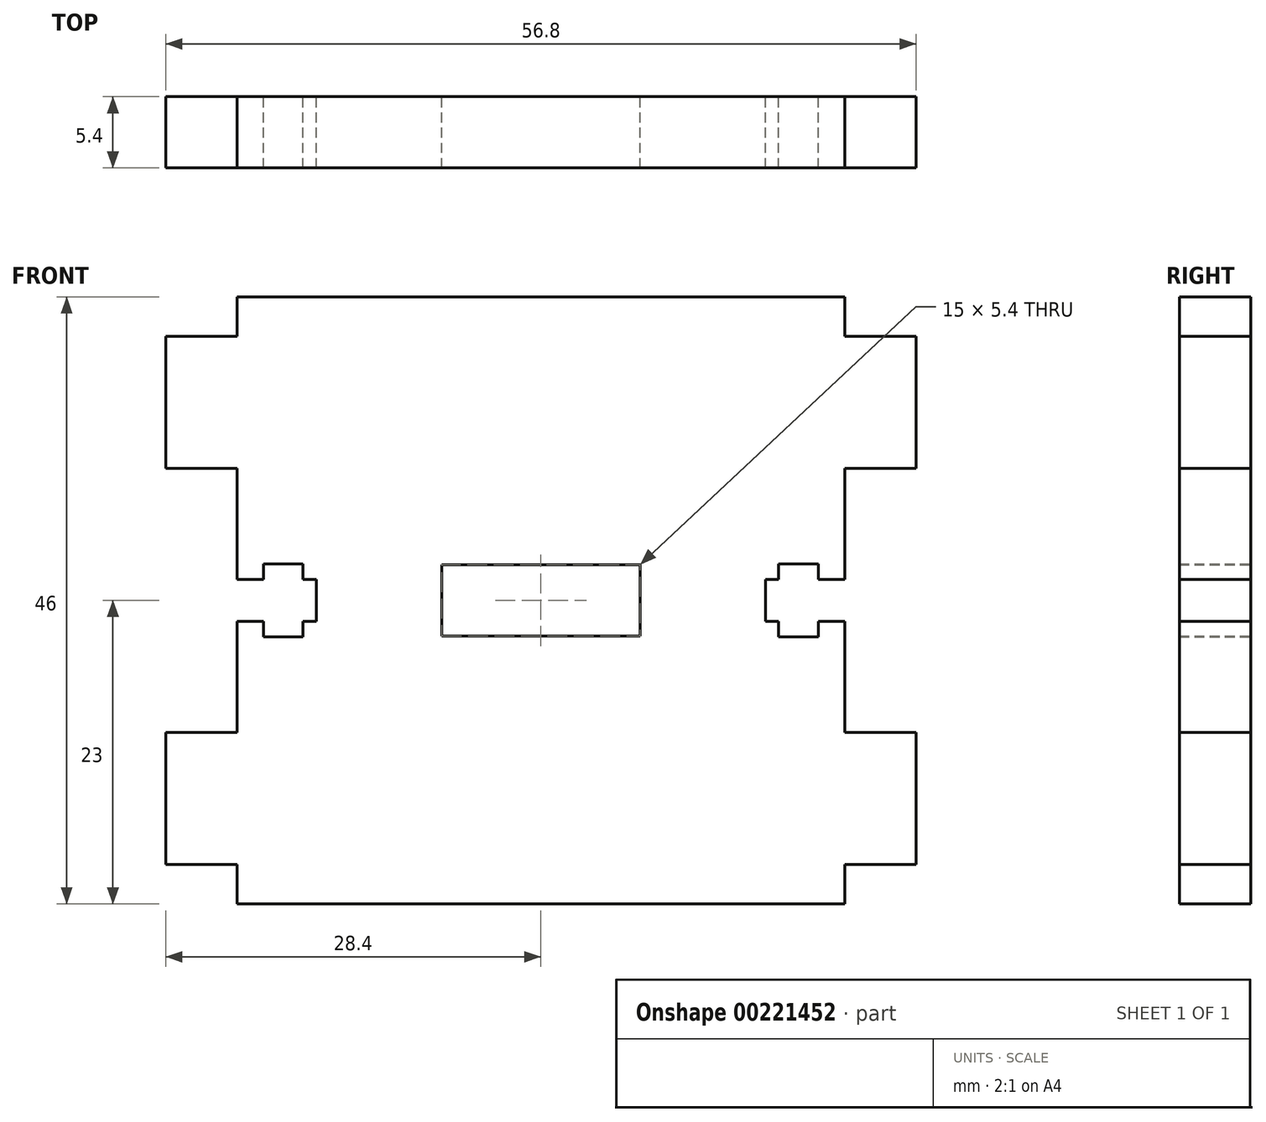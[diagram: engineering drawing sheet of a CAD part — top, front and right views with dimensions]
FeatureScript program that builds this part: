
annotation { "Feature Type Name" : "Feature", "Feature Type Description" : "" }
export const myFeature = defineFeature(function(context is Context, id is Id, definition is map)
    precondition{}
    {
        {
            assignVariable(context, id + "F0", {"name" : "thickness", "anyValue" : 5.4 * mm});
        }
        {
            var Q0;
            Q0=qCreatedBy(makeId("Front.planeOp"),FACE);
            var sketch = newSketch(context, id + "F1", { "sketchPlane" : qUnion([Q0])});
            skLineSegment(sketch, "E0.bottom", {"start": v(0, 0) * mm, "end": v(46, 0) * mm});
            skLineSegment(sketch, "E0.top", {"start": v(0, 46) * mm, "end": v(46, 46) * mm});
            skLineSegment(sketch, "E0.left", {"start": v(0, 0) * mm, "end": v(0, 3) * mm});
            skLineSegment(sketch, "E0.right", {"start": v(46, 0) * mm, "end": v(46, 3) * mm});
            skLineSegment(sketch, "E1", {"start": v(0, 43) * mm, "end": v(-5.4, 43) * mm});
            skLineSegment(sketch, "E2", {"start": v(-5.4, 43) * mm, "end": v(-5.4, 33) * mm});
            skLineSegment(sketch, "E3", {"start": v(-5.4, 33) * mm, "end": v(0, 33) * mm});
            skLineSegment(sketch, "E4", {"start": v(0, 23) * mm, "end": v(46, 23) * mm, "construction": true});
            skLineSegment(sketch, "E5", {"start": v(0, 24.6) * mm, "end": v(2, 24.6) * mm});
            skLineSegment(sketch, "E6", {"start": v(2, 24.6) * mm, "end": v(2, 25.75) * mm});
            skLineSegment(sketch, "E7", {"start": v(2, 25.75) * mm, "end": v(5, 25.75) * mm});
            skLineSegment(sketch, "E8", {"start": v(5, 25.75) * mm, "end": v(5, 24.6) * mm});
            skLineSegment(sketch, "E9", {"start": v(5, 24.6) * mm, "end": v(6, 24.6) * mm});
            skLineSegment(sketch, "E10", {"start": v(6, 24.6) * mm, "end": v(6, 23) * mm});
            skLineSegment(sketch, "E11.MirrorCS", {"start": v(-5.4, 3) * mm, "end": v(-5.4, 13) * mm});
            skLineSegment(sketch, "E12.MirrorCS", {"start": v(-5.4, 13) * mm, "end": v(0, 13) * mm});
            skLineSegment(sketch, "E13.MirrorCS", {"start": v(0, 3) * mm, "end": v(-5.4, 3) * mm});
            skLineSegment(sketch, "E14.MirrorCS", {"start": v(5, 21.4) * mm, "end": v(6, 21.4) * mm});
            skLineSegment(sketch, "E15.MirrorCS", {"start": v(5, 20.25) * mm, "end": v(5, 21.4) * mm});
            skLineSegment(sketch, "E16.MirrorCS", {"start": v(2, 20.25) * mm, "end": v(5, 20.25) * mm});
            skLineSegment(sketch, "E17.MirrorCS", {"start": v(2, 21.4) * mm, "end": v(2, 20.25) * mm});
            skLineSegment(sketch, "E18.MirrorCS", {"start": v(6, 21.4) * mm, "end": v(6, 23) * mm});
            skLineSegment(sketch, "E19.MirrorCS", {"start": v(0, 21.4) * mm, "end": v(2, 21.4) * mm});
            skLineSegment(sketch, "E20.trimOffspring", {"start": v(0, 24.6) * mm, "end": v(0, 33) * mm});
            skLineSegment(sketch, "E21.trimOffspring", {"start": v(0, 43) * mm, "end": v(0, 46) * mm});
            skLineSegment(sketch, "E22.trimOffspring", {"start": v(0, 13) * mm, "end": v(0, 21.4) * mm});
            skLineSegment(sketch, "E23", {"start": v(0, 24.6) * mm, "end": v(0, 21.4) * mm, "construction": true});
            skLineSegment(sketch, "E24", {"start": v(23, 46) * mm, "end": v(23, 0) * mm, "construction": true});
            skLineSegment(sketch, "E25.MirrorCS", {"start": v(51.4, 43) * mm, "end": v(51.4, 33) * mm});
            skLineSegment(sketch, "E26.MirrorCS", {"start": v(51.4, 33) * mm, "end": v(46, 33) * mm});
            skLineSegment(sketch, "E27.MirrorCS", {"start": v(46, 43) * mm, "end": v(51.4, 43) * mm});
            skLineSegment(sketch, "E28.MirrorCS", {"start": v(41, 20.25) * mm, "end": v(41, 21.4) * mm});
            skLineSegment(sketch, "E29.MirrorCS", {"start": v(41, 24.6) * mm, "end": v(40, 24.6) * mm});
            skLineSegment(sketch, "E30.MirrorCS", {"start": v(41, 25.75) * mm, "end": v(41, 24.6) * mm});
            skLineSegment(sketch, "E31.MirrorCS", {"start": v(44, 24.6) * mm, "end": v(44, 25.75) * mm});
            skLineSegment(sketch, "E32.MirrorCS", {"start": v(46, 24.6) * mm, "end": v(44, 24.6) * mm});
            skLineSegment(sketch, "E33.MirrorCS", {"start": v(46, 21.4) * mm, "end": v(44, 21.4) * mm});
            skLineSegment(sketch, "E34.MirrorCS", {"start": v(44, 21.4) * mm, "end": v(44, 20.25) * mm});
            skLineSegment(sketch, "E35.MirrorCS", {"start": v(40, 21.4) * mm, "end": v(40, 23) * mm});
            skLineSegment(sketch, "E36.MirrorCS", {"start": v(41, 21.4) * mm, "end": v(40, 21.4) * mm});
            skLineSegment(sketch, "E37.MirrorCS", {"start": v(40, 24.6) * mm, "end": v(40, 23) * mm});
            skLineSegment(sketch, "E38.MirrorCS", {"start": v(44, 25.75) * mm, "end": v(41, 25.75) * mm});
            skLineSegment(sketch, "E39.MirrorCS", {"start": v(44, 20.25) * mm, "end": v(41, 20.25) * mm});
            skLineSegment(sketch, "E40.MirrorCS", {"start": v(51.4, 3) * mm, "end": v(51.4, 13) * mm});
            skLineSegment(sketch, "E41.MirrorCS", {"start": v(51.4, 13) * mm, "end": v(46, 13) * mm});
            skLineSegment(sketch, "E42.MirrorCS", {"start": v(46, 3) * mm, "end": v(51.4, 3) * mm});
            skLineSegment(sketch, "E43.trimOffspring", {"start": v(46, 43) * mm, "end": v(46, 46) * mm});
            skLineSegment(sketch, "E44.trimOffspring", {"start": v(46, 13) * mm, "end": v(46, 21.4) * mm});
            skLineSegment(sketch, "E45.trimOffspring", {"start": v(46, 24.6) * mm, "end": v(46, 33) * mm});
            skLineSegment(sketch, "E46.bottom", {"start": v(15.5, 25.7) * mm, "end": v(30.5, 25.7) * mm});
            skLineSegment(sketch, "E46.top", {"start": v(15.5, 20.3) * mm, "end": v(30.5, 20.3) * mm});
            skLineSegment(sketch, "E46.left", {"start": v(15.5, 25.7) * mm, "end": v(15.5, 20.3) * mm});
            skLineSegment(sketch, "E46.right", {"start": v(30.5, 25.7) * mm, "end": v(30.5, 20.3) * mm});
            skPoint(sketch, "E47", {"position": v(30.5, 23) * mm});
            skPoint(sketch, "E48", {"position": v(23, 20.3) * mm});
            skSolve(sketch);
        }
        {
            var Q0;
            Q0 = qSketchRegion(id + "F1", true);
            extrude(context, id + "F2", {"entities" : qUnion([Q0]), "depth" : getVariable(context, 'thickness')});
        }
    });
